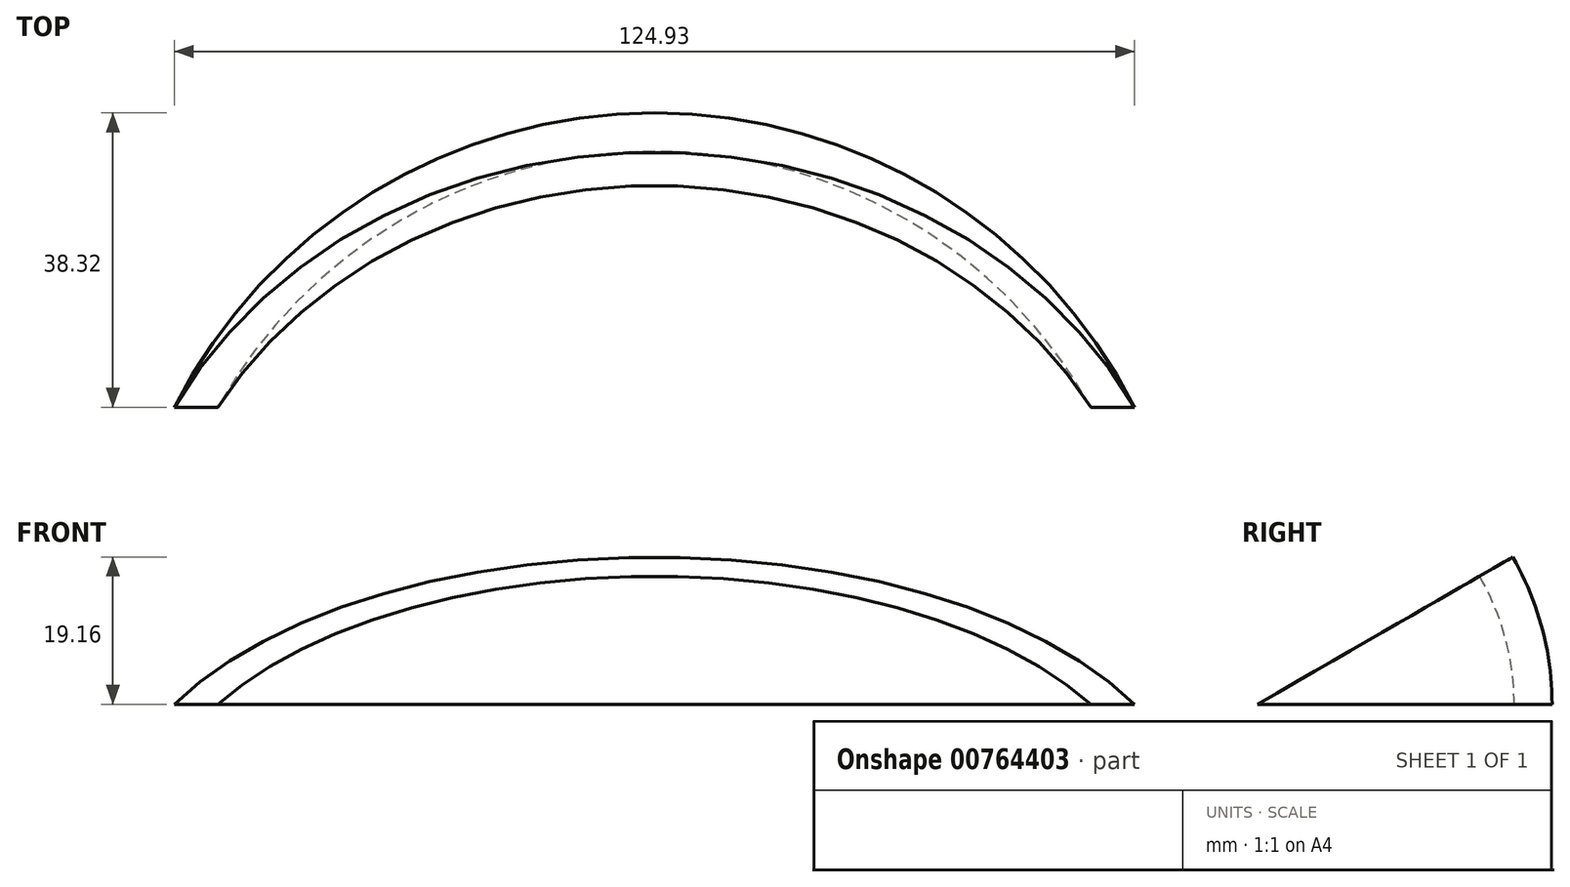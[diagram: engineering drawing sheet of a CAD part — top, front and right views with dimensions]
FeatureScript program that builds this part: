
annotation { "Feature Type Name" : "Feature", "Feature Type Description" : "" }
export const myFeature = defineFeature(function(context is Context, id is Id, definition is map)
    precondition{}
    {
        {
            var Q0;
            Q0=qCreatedBy(makeId("Top.planeOp"),FACE);
            var sketch = newSketch(context, id + "F0", { "sketchPlane" : qUnion([Q0])});
            skArc(sketch, "E0", {"start": v(63.6, 0) * mm, "mid": v(1.13, 38.32) * mm, "end": v(-61.33, 0) * mm});
            skLineSegment(sketch, "E1", {"start": v(-61.33, 0) * mm, "end": v(-55.67, 0) * mm});
            skArc(sketch, "E2.0", {"start": v(57.93, 0) * mm, "mid": v(1.13, 33.32) * mm, "end": v(-55.67, 0) * mm});
            skLineSegment(sketch, "E3.trimOffspring", {"start": v(57.93, 0) * mm, "end": v(63.6, 0) * mm});
            skLineSegment(sketch, "E4", {"start": v(-55.67, 0) * mm, "end": v(57.93, 0) * mm, "construction": true});
            skSolve(sketch);
        }
        {
            var Q0;
            Q0=makeQuery(id+"F0.imprint","IMPRINT",FACE,{"disambiguationData":[TD([[makeQuery(id+"F0.imprint","IMPRINT",EDGE,{"derivedFrom":sQuery(id+"F0.wireOp",EDGE,"E0")}),1.0]])]});
            var Q1;
            Q1=sQuery(id+"F0.wireOp",EDGE,"E1");
            revolve(context, id + "F1", {"surfaceOperationType" : NewSurfaceOperationType.NEW, "entities" : qUnion([Q0]), "axis" : qUnion([Q1]), "revolveType" : RevolveType.ONE_DIRECTION, "angle" : 30 * degree});
        }
    });
